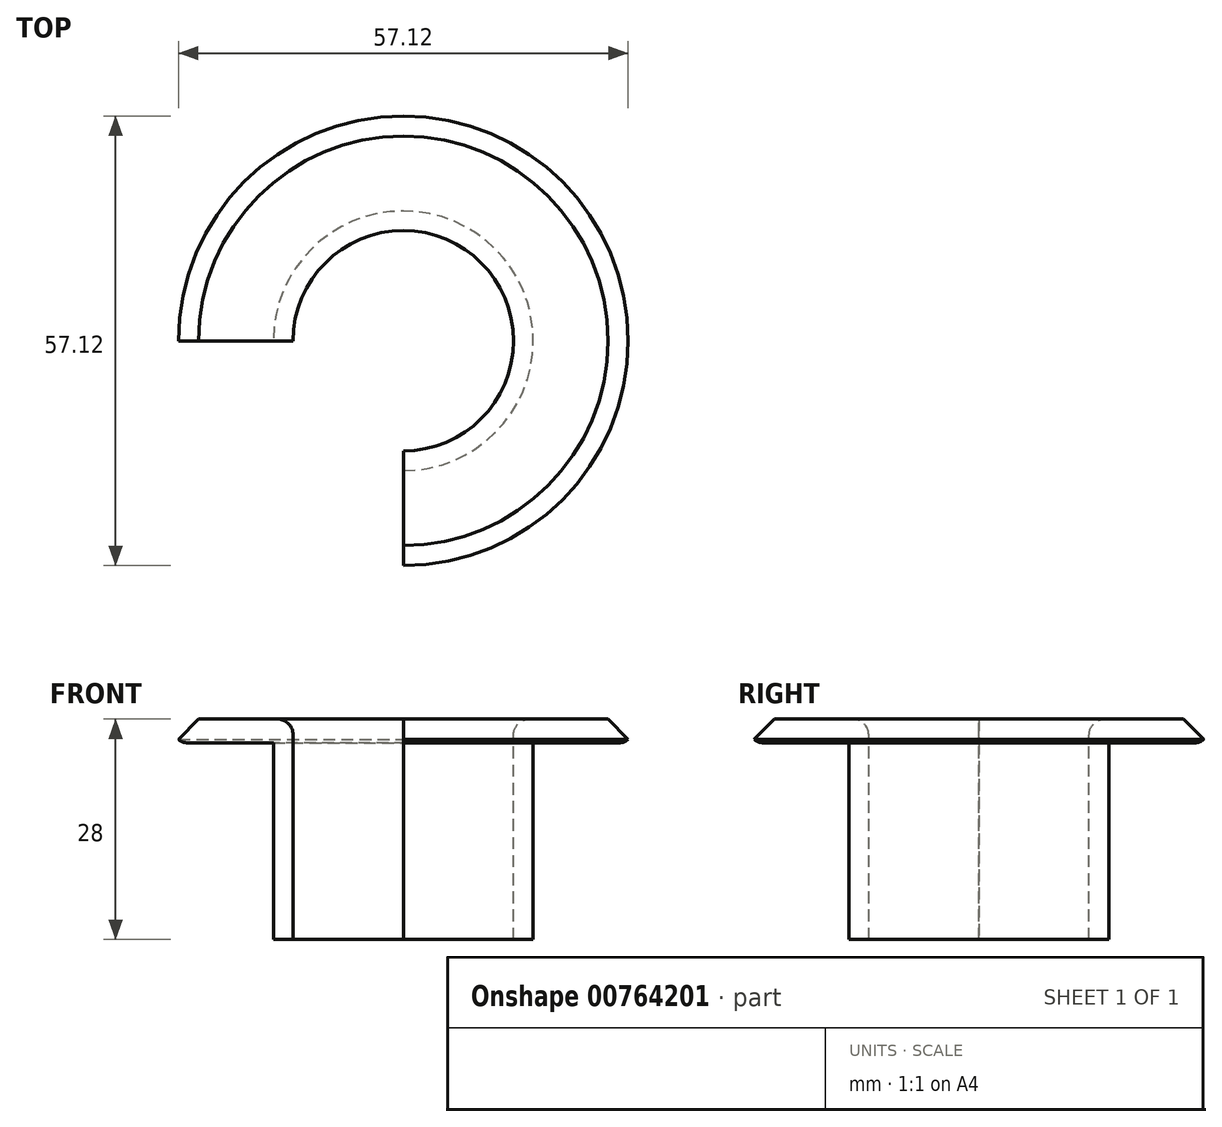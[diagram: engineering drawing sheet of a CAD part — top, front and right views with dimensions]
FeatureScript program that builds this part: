
annotation { "Feature Type Name" : "Feature", "Feature Type Description" : "" }
export const myFeature = defineFeature(function(context is Context, id is Id, definition is map)
    precondition{}
    {
        {
            var Q0;
            Q0=qCreatedBy(makeId("Front.planeOp"),FACE);
            var sketch = newSketch(context, id + "F0", { "sketchPlane" : qUnion([Q0])});
            skLineSegment(sketch, "E0", {"start": v(0, 0) * mm, "end": v(0, 28) * mm});
            skLineSegment(sketch, "E1", {"start": v(0, 28) * mm, "end": v(-15, 28) * mm});
            skLineSegment(sketch, "E2", {"start": v(-15, 28) * mm, "end": v(-15, 25) * mm});
            skLineSegment(sketch, "E3", {"start": v(-15, 25) * mm, "end": v(-12.5, 25) * mm});
            skLineSegment(sketch, "E4", {"start": v(-12.5, 25) * mm, "end": v(-12.5, 25) * mm});
            skLineSegment(sketch, "E5", {"start": v(-12.5, 25) * mm, "end": v(-2.5, 25) * mm});
            skLineSegment(sketch, "E6", {"start": v(-2.5, 25) * mm, "end": v(-2.5, 0) * mm});
            skLineSegment(sketch, "E7", {"start": v(-2.5, 0) * mm, "end": v(0, 0) * mm});
            skLineSegment(sketch, "E8", {"start": v(14, 52.32) * mm, "end": v(14, -58.62) * mm, "construction": true});
            skSolve(sketch);
        }
        {
            var Q0;
            Q0=makeQuery(id+"F0.imprint","IMPRINT",FACE,{"disambiguationData":[TD([[makeQuery(id+"F0.imprint","IMPRINT",EDGE,{"derivedFrom":sQuery(id+"F0.wireOp",EDGE,"E0")}),1.0]])]});
            var Q1;
            Q1=sQuery(id+"F0.wireOp",EDGE,"E8");
            revolve(context, id + "F1", {"surfaceOperationType" : NewSurfaceOperationType.NEW, "entities" : qUnion([Q0]), "axis" : qUnion([Q1]), "revolveType" : RevolveType.ONE_DIRECTION, "angle" : 270 * degree});
        }
        {
            var Q0;
            Q0=makeQuery(id+"F1.opRevolve","SWEPT_EDGE",EDGE,{"disambiguationData":[OSD([sQuery(id+"F0.wireOp",EDGE,"E3"),sQuery(id+"F0.wireOp",EDGE,"E4")])]});
            fillet(context, id + "F2", {"entities" : qUnion([Q0]), "radius" : 1.5 * mm, "tangentPropagation" : true, "allowEdgeOverflow" : false});
        }
        {
            var Q0;
            Q0=makeQuery(id+"F1.opRevolve","SWEPT_EDGE",EDGE,{"disambiguationData":[OSD([sQuery(id+"F0.wireOp",EDGE,"E1"),sQuery(id+"F0.wireOp",EDGE,"E2")])]});
            chamfer(context, id + "F3", {"entities" : qUnion([Q0]), "width" : 3 * mm, "tangentPropagation" : true});
        }
        {
            var Q0;
            Q0=makeQuery(id+"F1.opRevolve","SWEPT_EDGE",EDGE,{"disambiguationData":[OSD([sQuery(id+"F0.wireOp",EDGE,"E0"),sQuery(id+"F0.wireOp",EDGE,"E1")])]});
            fillet(context, id + "F4", {"entities" : qUnion([Q0]), "radius" : 2 * mm, "tangentPropagation" : true, "allowEdgeOverflow" : false});
        }
    });
